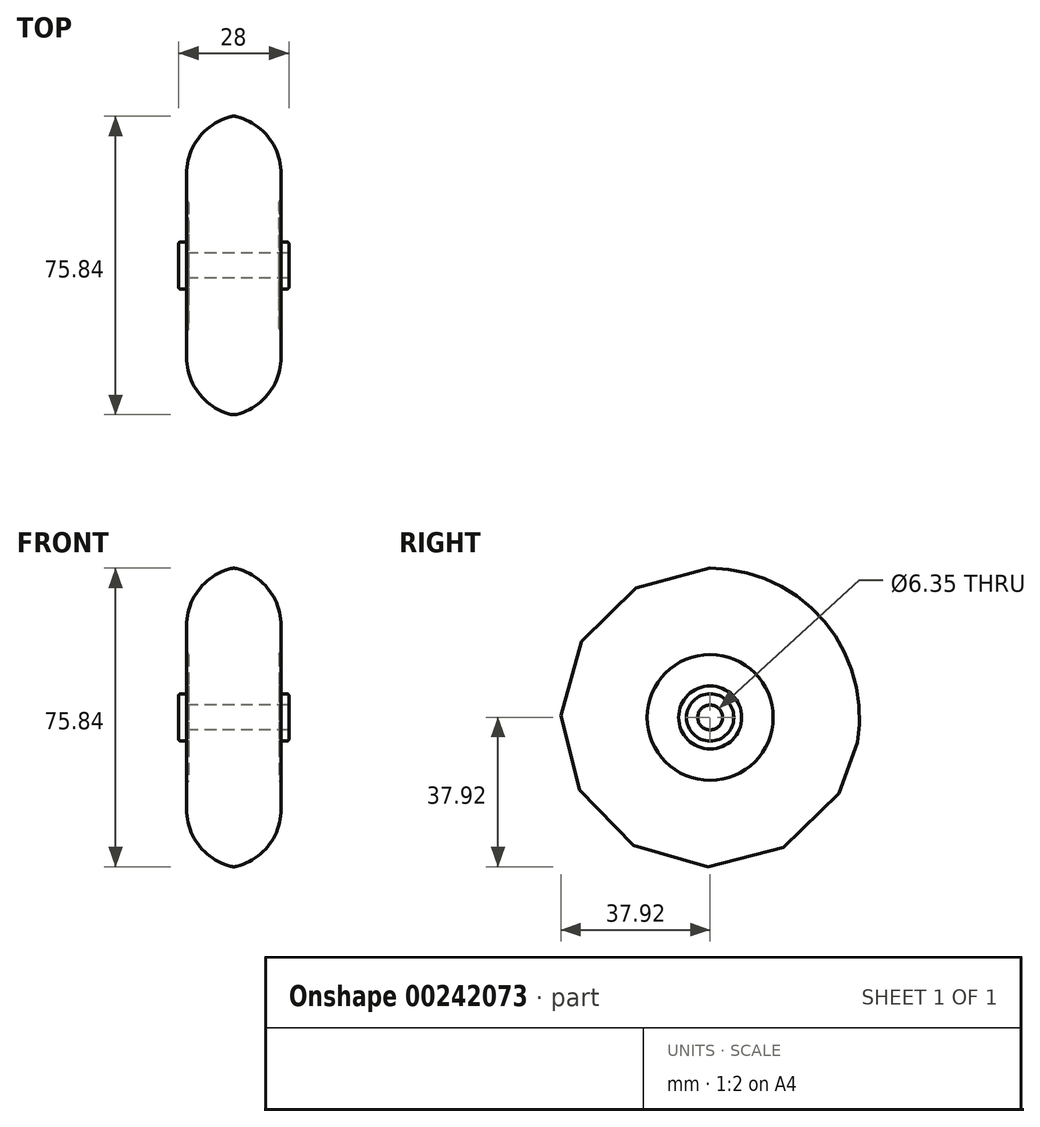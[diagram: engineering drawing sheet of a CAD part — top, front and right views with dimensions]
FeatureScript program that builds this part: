
annotation { "Feature Type Name" : "Feature", "Feature Type Description" : "" }
export const myFeature = defineFeature(function(context is Context, id is Id, definition is map)
    precondition{}
    {
        {
            var Q0;
            Q0=qCreatedBy(makeId("Front.planeOp"),FACE);
            var sketch = newSketch(context, id + "F0", { "sketchPlane" : qUnion([Q0])});
            skLineSegment(sketch, "E0", {"start": v(-13.97, 0) * mm, "end": v(13.97, 0) * mm, "construction": true});
            skPoint(sketch, "E1", {"position": v(0, 0) * mm});
            skLineSegment(sketch, "E2", {"start": v(0, 3.18) * mm, "end": v(-14, 3.18) * mm});
            skLineSegment(sketch, "E3", {"start": v(-14, 3.17) * mm, "end": v(-14, 5.5) * mm});
            skLineSegment(sketch, "E4", {"start": v(-13.5, 6) * mm, "end": v(-12, 6) * mm});
            skLineSegment(sketch, "E5", {"start": v(-12, 6) * mm, "end": v(-12, 8) * mm});
            skLineSegment(sketch, "E6", {"start": v(-12, 8) * mm, "end": v(-11.5, 8) * mm});
            skLineSegment(sketch, "E7", {"start": v(-11.5, 8) * mm, "end": v(-11.5, 16) * mm});
            skLineSegment(sketch, "E8", {"start": v(-11.5, 16) * mm, "end": v(-11.73, 16.4) * mm});
            skLineSegment(sketch, "E9", {"start": v(-12, 17.4) * mm, "end": v(-12, 23.3) * mm});
            skArc(sketch, "E10", {"start": v(0, 38) * mm, "mid": v(-8.62, 32.79) * mm, "end": v(-12, 23.3) * mm});
            skPoint(sketch, "E11.visualSharp", {"position": v(-12, 16.87) * mm});
            skArc(sketch, "E11.filletArc", {"start": v(-12, 17.4) * mm, "mid": v(-11.93, 16.88) * mm, "end": v(-11.73, 16.4) * mm});
            skLineSegment(sketch, "E12", {"start": v(0, 38) * mm, "end": v(0, 0) * mm, "construction": true});
            skPoint(sketch, "E13.visualSharp", {"position": v(-14, 6) * mm});
            skArc(sketch, "E13.filletArc", {"start": v(-13.5, 6) * mm, "mid": v(-13.85, 5.85) * mm, "end": v(-14, 5.5) * mm});
            skArc(sketch, "E14.MirrorCS", {"start": v(13.5, 6) * mm, "mid": v(13.85, 5.85) * mm, "end": v(14, 5.5) * mm});
            skLineSegment(sketch, "E15.MirrorCS", {"start": v(13.5, 6) * mm, "end": v(12, 6) * mm});
            skLineSegment(sketch, "E16.MirrorCS", {"start": v(11.5, 16) * mm, "end": v(11.73, 16.4) * mm});
            skArc(sketch, "E17.MirrorCS", {"start": v(12, 17.4) * mm, "mid": v(11.93, 16.88) * mm, "end": v(11.73, 16.4) * mm});
            skLineSegment(sketch, "E18.MirrorCS", {"start": v(14, 3.17) * mm, "end": v(14, 5.5) * mm});
            skLineSegment(sketch, "E19.MirrorCS", {"start": v(12, 6) * mm, "end": v(12, 8) * mm});
            skLineSegment(sketch, "E20.MirrorCS", {"start": v(12, 8) * mm, "end": v(11.5, 8) * mm});
            skPoint(sketch, "E21.MirrorP", {"position": v(12, 16.87) * mm});
            skLineSegment(sketch, "E22.MirrorCS", {"start": v(0, 3.18) * mm, "end": v(14, 3.17) * mm});
            skPoint(sketch, "E23.MirrorP", {"position": v(14, 6) * mm});
            skLineSegment(sketch, "E24.MirrorCS", {"start": v(11.5, 8) * mm, "end": v(11.5, 16) * mm});
            skLineSegment(sketch, "E25.MirrorCS", {"start": v(12, 17.4) * mm, "end": v(12, 23.3) * mm});
            skArc(sketch, "E26.MirrorCS", {"start": v(0, 38) * mm, "mid": v(8.62, 32.79) * mm, "end": v(12, 23.3) * mm});
            skSolve(sketch);
        }
        {
            var Q0;
            Q0=qSketchRegion(id+"F0",true);
            var Q1;
            Q1=sQuery(id+"F0.wireOp",EDGE,"E0");
            revolve(context, id + "F1", {"entities" : qUnion([Q0]), "axis" : qUnion([Q1]), "revolveType" : RevolveType.FULL});
        }
        {
            var Q0;
            Q0=makeQuery(id+"F1.opRevolve","SWEPT_EDGE",EDGE,{"disambiguationData":[OSD([sQuery(id+"F0.wireOp",EDGE,"E10"),sQuery(id+"F0.wireOp",EDGE,"E26.MirrorCS")])]});
            fillet(context, id + "F2", {"entities" : qUnion([Q0]), "radius" : 3 * mm, "tangentPropagation" : true, "allowEdgeOverflow" : false});
        }
    });
